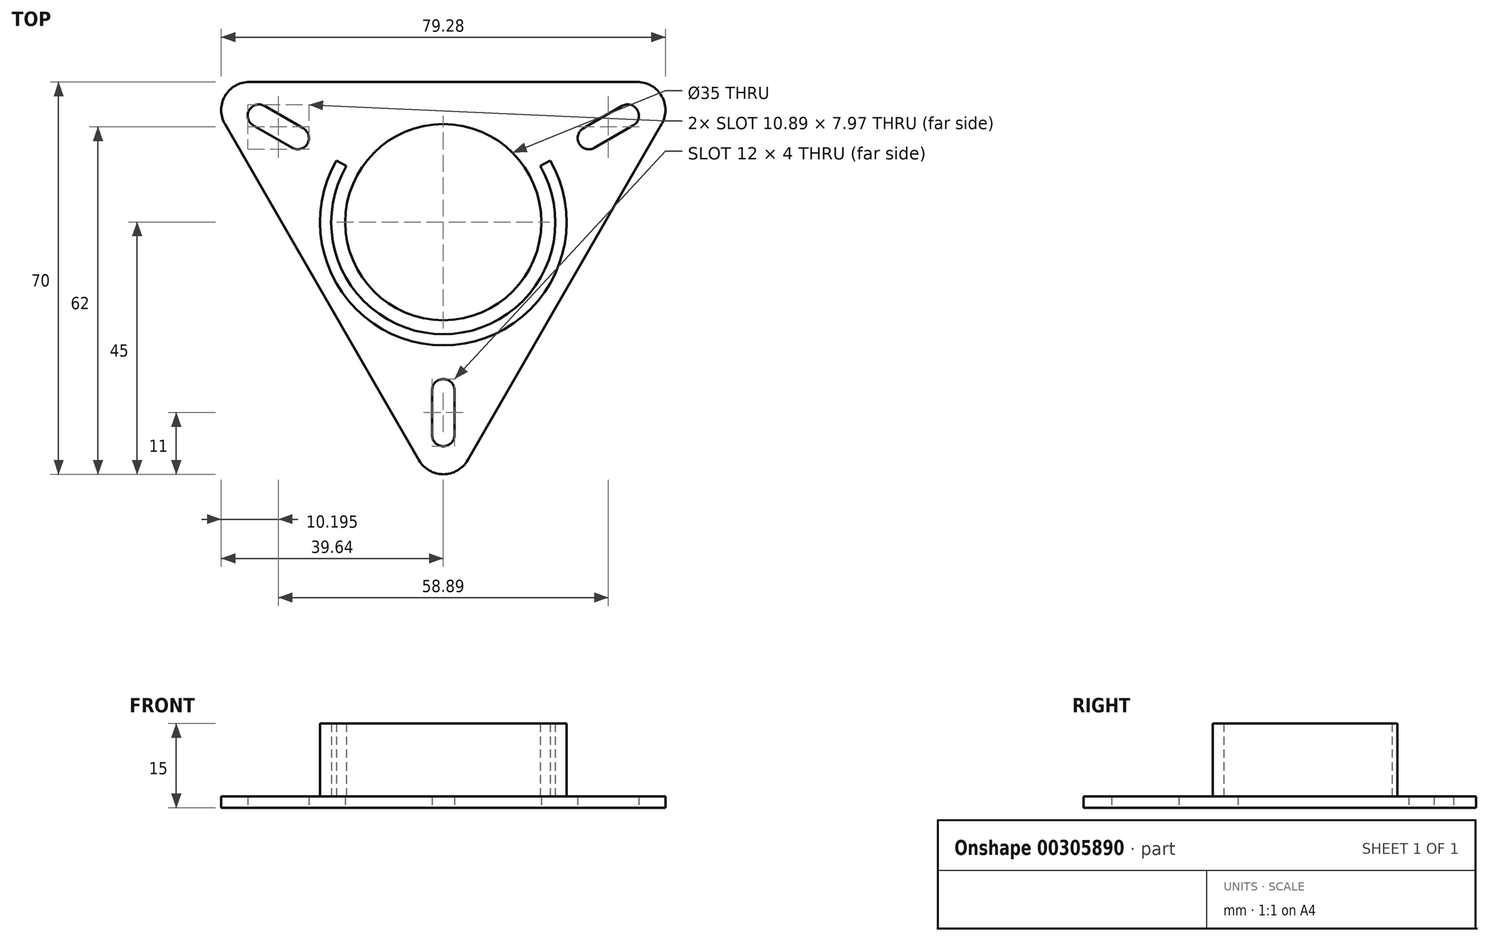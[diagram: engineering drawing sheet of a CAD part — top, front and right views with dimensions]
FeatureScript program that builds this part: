
annotation { "Feature Type Name" : "Feature", "Feature Type Description" : "" }
export const myFeature = defineFeature(function(context is Context, id is Id, definition is map)
    precondition{}
    {
        {
            var Q0;
            Q0=qCreatedBy(makeId("Top.planeOp"),FACE);
            var sketch = newSketch(context, id + "F0", { "sketchPlane" : qUnion([Q0])});
            skCircle(sketch, "E0.cCircle", {"center": v(0, 0) * mm, "radius": 25 * mm, "construction": true});
            skLineSegment(sketch, "E0.0", {"start": v(-34.64, 25) * mm, "end": v(34.64, 25) * mm});
            skLineSegment(sketch, "E0.1", {"start": v(38.97, 17.5) * mm, "end": v(4.33, -42.5) * mm});
            skLineSegment(sketch, "E0.2", {"start": v(-4.33, -42.5) * mm, "end": v(-38.97, 17.5) * mm});
            skPoint(sketch, "E0.0.midPoint", {"position": v(0, 25) * mm});
            skArc(sketch, "E1", {"start": v(-17.32, 10) * mm, "mid": v(0, -20) * mm, "end": v(17.32, 10) * mm});
            skArc(sketch, "E2", {"start": v(-19.05, 11) * mm, "mid": v(0, -22) * mm, "end": v(19.05, 11) * mm});
            skLineSegment(sketch, "E3", {"start": v(0, 0) * mm, "end": v(0, 42.42) * mm, "construction": true});
            skLineSegment(sketch, "E4", {"start": v(0, 0) * mm, "end": v(-43.3, 25) * mm, "construction": true});
            skLineSegment(sketch, "E5", {"start": v(0, 0) * mm, "end": v(43.3, 25) * mm, "construction": true});
            skLineSegment(sketch, "E6", {"start": v(0, 0) * mm, "end": v(0, -50) * mm, "construction": true});
            skPoint(sketch, "E7.visualSharp", {"position": v(-43.3, 25) * mm});
            skArc(sketch, "E7.filletArc", {"start": v(-34.64, 25) * mm, "mid": v(-38.97, 22.5) * mm, "end": v(-38.97, 17.5) * mm});
            skPoint(sketch, "E8.visualSharp", {"position": v(43.3, 25) * mm});
            skArc(sketch, "E8.filletArc", {"start": v(38.97, 17.5) * mm, "mid": v(38.97, 22.5) * mm, "end": v(34.64, 25) * mm});
            skPoint(sketch, "E9.visualSharp", {"position": v(0, -50) * mm});
            skArc(sketch, "E9.filletArc", {"start": v(-4.33, -42.5) * mm, "mid": v(0, -45) * mm, "end": v(4.33, -42.5) * mm});
            skLineSegment(sketch, "E10", {"start": v(-17.32, 10) * mm, "end": v(-19.05, 11) * mm});
            skLineSegment(sketch, "E11", {"start": v(17.32, 10) * mm, "end": v(19.05, 11) * mm});
            skLineSegment(sketch, "E12", {"start": v(-31.9, 20.73) * mm, "end": v(-24.98, 16.73) * mm});
            skLineSegment(sketch, "E13", {"start": v(-33.9, 17.27) * mm, "end": v(-26.98, 13.27) * mm});
            skArc(sketch, "E14", {"start": v(-31.9, 20.73) * mm, "mid": v(-34.64, 20) * mm, "end": v(-33.9, 17.27) * mm});
            skArc(sketch, "E15", {"start": v(-26.98, 13.27) * mm, "mid": v(-24.25, 14) * mm, "end": v(-24.98, 16.73) * mm});
            skLineSegment(sketch, "E16.1.0", {"start": v(-2, -38) * mm, "end": v(-2, -30) * mm});
            skArc(sketch, "E16.1.1", {"start": v(-2, -38) * mm, "mid": v(0, -40) * mm, "end": v(2, -38) * mm});
            skArc(sketch, "E16.1.2", {"start": v(2, -30) * mm, "mid": v(0, -28) * mm, "end": v(-2, -30) * mm});
            skLineSegment(sketch, "E16.1.3", {"start": v(2, -38) * mm, "end": v(2, -30) * mm});
            skLineSegment(sketch, "E16.2.0", {"start": v(33.9, 17.27) * mm, "end": v(26.98, 13.27) * mm});
            skArc(sketch, "E16.2.1", {"start": v(33.9, 17.27) * mm, "mid": v(34.64, 20) * mm, "end": v(31.9, 20.73) * mm});
            skArc(sketch, "E16.2.2", {"start": v(24.98, 16.73) * mm, "mid": v(24.25, 14) * mm, "end": v(26.98, 13.27) * mm});
            skLineSegment(sketch, "E16.2.3", {"start": v(31.9, 20.73) * mm, "end": v(24.98, 16.73) * mm});
            skCircle(sketch, "E17", {"center": v(0, 0) * mm, "radius": 17.5 * mm});
            skCircle(sketch, "E18", {"center": v(0, 0) * mm, "radius": 15.5 * mm});
            skSolve(sketch);
        }
        {
            var Q0;
            Q0=makeQuery(id+"F0.imprint","IMPRINT",FACE,{"disambiguationData":[TD([[makeQuery(id+"F0.imprint","IMPRINT",EDGE,{"derivedFrom":sQuery(id+"F0.wireOp",EDGE,"E0.0")}),-1.0]])]});
            extrude(context, id + "F1", {"entities" : qUnion([Q0]), "depth" : 2 * mm});
        }
        {
            var Q0;
            Q0=makeQuery(id+"F0.imprint","IMPRINT",FACE,{"disambiguationData":[TD([[makeQuery(id+"F0.imprint","IMPRINT",EDGE,{"derivedFrom":sQuery(id+"F0.wireOp",EDGE,"E1")}),-1.0]])]});
            extrude(context, id + "F2", {"entities" : qUnion([Q0]), "operationType" : NewBodyOperationType.ADD, "depth" : 15 * mm});
        }
    });
